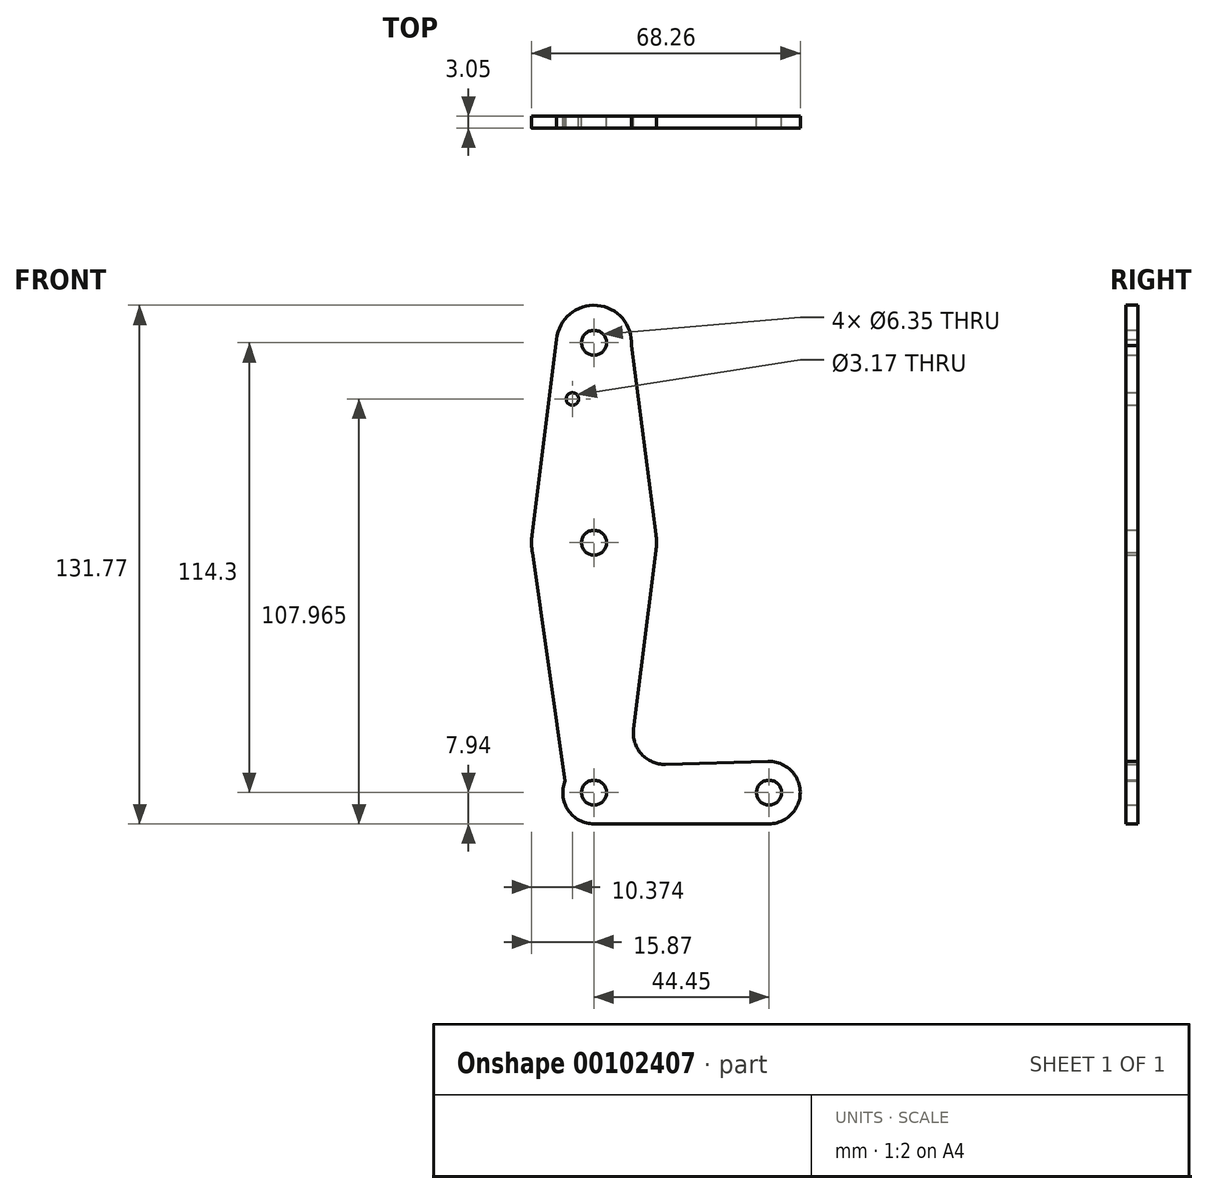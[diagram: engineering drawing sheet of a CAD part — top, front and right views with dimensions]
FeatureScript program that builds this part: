
annotation { "Feature Type Name" : "Feature", "Feature Type Description" : "" }
export const myFeature = defineFeature(function(context is Context, id is Id, definition is map)
    precondition{}
    {
        {
            var Q0;
            Q0=qCreatedBy(makeId("Front.planeOp"),FACE);
            var sketch = newSketch(context, id + "F0", { "sketchPlane" : qUnion([Q0])});
            skLineSegment(sketch, "E0", {"start": v(0, 0) * mm, "end": v(0, 114.3) * mm});
            skCircle(sketch, "E1", {"center": v(0, 114.3) * mm, "radius": 9.53 * mm});
            skCircle(sketch, "E2", {"center": v(0, 63.5) * mm, "radius": 15.88 * mm});
            skLineSegment(sketch, "E3", {"start": v(0, 0) * mm, "end": v(44.45, 0) * mm});
            skCircle(sketch, "E4", {"center": v(0, 0) * mm, "radius": 7.94 * mm});
            skCircle(sketch, "E5", {"center": v(44.45, 0) * mm, "radius": 7.94 * mm});
            skLineSegment(sketch, "E6", {"start": v(-9.49, 115.15) * mm, "end": v(-15.75, 65.49) * mm});
            skLineSegment(sketch, "E7", {"start": v(9.5, 113.63) * mm, "end": v(15.74, 65.54) * mm});
            skLineSegment(sketch, "E8", {"start": v(15.75, 61.52) * mm, "end": v(10.03, 16.13) * mm});
            skLineSegment(sketch, "E9", {"start": v(18.15, 7.19) * mm, "end": v(44.22, 7.93) * mm});
            skLineSegment(sketch, "E10", {"start": v(0, -7.94) * mm, "end": v(44.45, -7.94) * mm});
            skLineSegment(sketch, "E11", {"start": v(-15.75, 61.51) * mm, "end": v(-7.35, 3) * mm});
            skPoint(sketch, "E12.newPointA", {"position": v(8, 0) * mm});
            skArc(sketch, "E12.filletArc", {"start": v(10.03, 16.13) * mm, "mid": v(12.03, 9.8) * mm, "end": v(18.15, 7.19) * mm});
            skCircle(sketch, "E13", {"center": v(0, 114.3) * mm, "radius": 3.18 * mm});
            skCircle(sketch, "E14", {"center": v(-5.5, 100.03) * mm, "radius": 1.59 * mm});
            skCircle(sketch, "E15", {"center": v(0, 63.5) * mm, "radius": 3.18 * mm});
            skCircle(sketch, "E16", {"center": v(0, 0) * mm, "radius": 3.18 * mm});
            skCircle(sketch, "E17", {"center": v(44.45, 0) * mm, "radius": 3.18 * mm});
            skSolve(sketch);
        }
        {
            var Q0;
            Q0 = qSketchRegion(id + "F0", true);
            var Q1;
            {var subQ0=sQuery(id+"F0.wireOp",EDGE,"E16");var subQ1=sQuery(id+"F0.wireOp",EDGE,"E0");var subQ2=makeQuery(id+"F0.imprint","INTERSECT",VERTEX,{"derivedFrom":[subQ1,subQ0]});Q1=makeQuery(id+"F0.imprint","IMPRINT",FACE,{"disambiguationData":[TD([[makeQuery(id+"F0.imprint","IMPRINT",EDGE,{"disambiguationData":[TD([[subQ2,-1.0]])],"derivedFrom":subQ1}),-1.0]])]});}
            extrude(context, id + "F1", {"entities" : qUnion([Q0, Q1]), "depth" : 3.05 * mm});
        }
    });
